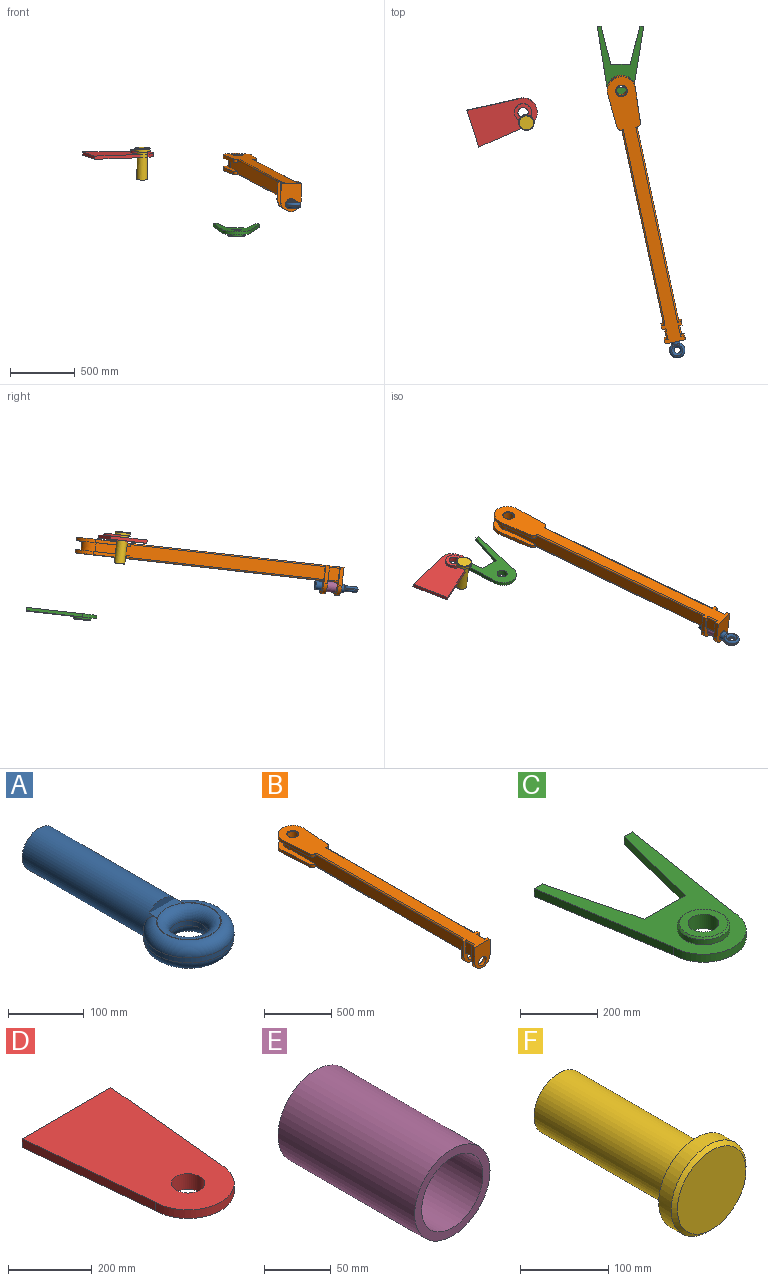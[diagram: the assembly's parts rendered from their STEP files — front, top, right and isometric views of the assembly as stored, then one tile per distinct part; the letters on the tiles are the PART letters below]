
ASSEMBLY  parts=6 mates=6
PART A: 12 faces, bbox 129.9x344.9x64 mm
  f0: cylinder r=32mm len=244.42mm, axis (0,1,0), area 46375.5mm2, adj f1,f2,f3,f4,f5,f6,f9,f11
  f1: plane 48.29x11mm, normal (0,-1,0), area 368.4mm2, adj f0,f5
  f2: plane 48.29x11mm, normal (0,-1,0), area 368.4mm2, adj f0,f6
  f3: plane 64x64mm, normal (0,1,0), area 3217mm2, adj f0
  f4: cylinder r=60mm len=120mm, axis (0,0,1), area 2477.5mm2, adj f0,f9,f11
  f5: plane 93x86mm, normal (0,0,-1), area 720mm2, adj f0,f1,f10,f11
  f6: plane 93x86mm, normal (0,0,1), area 720mm2, adj f0,f2,f8,f9
  f7: cylinder r=25mm len=50mm, axis (0,0,1), area 1256.6mm2, adj f8,f10
  f8: torus R=42mm, axis (0,0,1), area 5231.1mm2, adj f6,f7
  f9: torus R=43mm, axis (0,0,1), area 7473.2mm2, adj f0,f4,f6
  f10: torus R=42mm, axis (0,0,1), area 5231.1mm2, adj f5,f7
  f11: torus R=43mm, axis (0,0,1), area 7473.2mm2, adj f0,f4,f5
PART B: 63 faces, bbox 220x2110x220 mm
  f0: plane 100x85mm, normal (1,0,0), area 8500mm2, adj f23,f26,f36,f37
  f1: plane 100x85mm, normal (-1,0,0), area 8500mm2, adj f23,f26,f35,f38
  f2: plane 100x85mm, normal (0,0,-1), area 8500mm2, adj f23,f26,f35,f36
  f3: plane 1824.08x100mm, normal (1,0,0), area 174335.4mm2, adj f6,f12,f13,f18,f19,f22,f31,f33
  f4: plane 1824.08x100mm, normal (-1,0,0), area 174335.4mm2, adj f6,f12,f14,f18,f20,f22,f32,f34
  f5: plane 1965x220mm, normal (0,0,-1), area 227854.4mm2, adj f15,f16,f17,f19,f20,f22,f32,f33
  f6: cylinder r=67.5mm len=135mm, axis (0,0,1), area 19341.1mm2, adj f3,f4,f12,f18
  f7: plane 2110x220mm, normal (0,0,1), area 245919.5mm2, adj f8,f9,f10,f11,f13,f14,f22,f23
  f8: plane 220x160mm, normal (0,-1,0), area 27426.5mm2, adj f7,f27,f28,f29,f39
  f9: plane 257.39x25mm, normal (1,-0.07,0), area 6449.1mm2, adj f7,f11,f12,f44
  f10: plane 257.39x25mm, normal (-1,-0.07,0), area 6449.1mm2, adj f7,f11,f12,f43
  f11: cylinder r=110mm len=220mm, axis (0,0,1), area 9371.6mm2, adj f7,f9,f10,f12
  f12: plane 410x220mm, normal (0,0,-1), area 35211.4mm2, adj f3,f4,f6,f9,f10,f11,f13,f14
  f13: plane 25x11.93mm, normal (0,-1,0), area 69.8mm2, adj f3,f7,f12,f31,f44
  f14: plane 25x11.93mm, normal (0,-1,0), area 69.8mm2, adj f4,f7,f12,f34,f43
  f15: plane 264.61x25mm, normal (-1,-0.07,0), area 6630.4mm2, adj f5,f17,f18,f42
  f16: plane 257.39x25mm, normal (1,-0.07,0), area 6449.1mm2, adj f5,f17,f18,f41
  f17: cylinder r=110mm len=220mm, axis (0,0,-1), area 9190.9mm2, adj f5,f15,f16,f18
  f18: plane 410x220mm, normal (0,0,1), area 35246.3mm2, adj f3,f4,f6,f15,f16,f17,f19,f20
  f19: plane 25x11.93mm, normal (0,-1,0), area 69.8mm2, adj f3,f5,f18,f33,f41
  f20: plane 25x11.96mm, normal (0,-1,0), area 70.4mm2, adj f4,f5,f18,f32,f42
  f21: cylinder r=40mm len=110mm, axis (0,0,1), area 27646mm2, adj f45,f46
  f22: plane 220x160mm, normal (0,1,0), area 13112.4mm2, adj f3,f4,f5,f7,f24,f25,f30,f31
  f23: plane 220x160mm, normal (0,-1,0), area 13112.4mm2, adj f0,f1,f2,f7,f24,f25,f30,f35
  f24: plane 140x30mm, normal (-1,0,0), area 4200mm2, adj f7,f22,f23,f40
  f25: plane 140x30mm, normal (1,0,0), area 4200mm2, adj f7,f22,f23,f40
  f26: plane 220x160mm, normal (0,1,0), area 13112.4mm2, adj f0,f1,f2,f7,f27,f28,f29,f35
  f27: plane 140x30mm, normal (-1,0,0), area 4200mm2, adj f7,f8,f26,f39
  f28: plane 140x30mm, normal (1,0,0), area 4200mm2, adj f7,f8,f26,f39
  f29: cylinder r=40mm len=80mm, axis (0,-1,0), area 7539.8mm2, adj f8,f26
  f30: cylinder r=40mm len=80mm, axis (0,-1,0), area 7539.8mm2, adj f22,f23
  f31: cylinder r=10mm len=1555mm, axis (0,1,0), area 24425.9mm2, adj f3,f7,f13,f22
  f32: cylinder r=10mm len=1555mm, axis (0,1,0), area 24425.9mm2, adj f4,f5,f20,f22
  f33: cylinder r=10mm len=1555mm, axis (0,-1,0), area 24425.9mm2, adj f3,f5,f19,f22
  f34: cylinder r=10mm len=1555mm, axis (0,-1,0), area 24425.9mm2, adj f4,f7,f14,f22
  f35: cylinder r=10mm len=85mm, axis (0,1,0), area 1335.2mm2, adj f1,f2,f23,f26
  f36: cylinder r=10mm len=85mm, axis (0,-1,0), area 1335.2mm2, adj f0,f2,f23,f26
  f37: cylinder r=10mm len=85mm, axis (0,1,0), area 1335.2mm2, adj f0,f7,f23,f26
  f38: cylinder r=10mm len=85mm, axis (0,-1,0), area 1335.2mm2, adj f1,f7,f23,f26
  f39: cylinder r=80mm len=160mm, axis (0,-1,0), area 7539.8mm2, adj f8,f26,f27,f28
  f40: cylinder r=80mm len=160mm, axis (0,-1,0), area 7539.8mm2, adj f22,f23,f24,f25
  f41: cylinder r=30mm len=29.93mm, axis (0,0,-1), area 1128.2mm2, adj f5,f16,f18,f19
  f42: cylinder r=30mm len=29.93mm, axis (0,0,-1), area 1127.5mm2, adj f5,f15,f18,f20
  f43: cylinder r=30mm len=29.93mm, axis (0,0,1), area 1128.2mm2, adj f7,f10,f12,f14
  f44: cylinder r=30mm len=29.93mm, axis (0,0,1), area 1128.2mm2, adj f7,f9,f12,f13
  f45: cone r=40mm half-angle=45deg, axis (0,0,-1), area 1888.2mm2, adj f5,f21
  f46: cone r=40mm half-angle=45deg, axis (0,0,1), area 1888.2mm2, adj f7,f21
  f47: plane 100x100mm, normal (0,1,0), area 10000mm2, adj f49,f50,f51,f52
  f48: plane 100x100mm, normal (0,-1,0), area 10000mm2, adj f49,f50,f51,f52
  f49: plane 100x85mm, normal (-1,0,0), area 8500mm2, adj f47,f48,f50,f52
  f50: plane 100x85mm, normal (0,0,-1), area 8500mm2, adj f47,f48,f49,f51
  f51: plane 100x85mm, normal (1,0,0), area 8500mm2, adj f47,f48,f50,f52
  f52: plane 100x85mm, normal (0,0,1), area 8500mm2, adj f47,f48,f49,f51
  f53: plane 100x100mm, normal (0,1,0), area 10000mm2, adj f59,f60,f61,f62
  f54: plane 100x15mm, normal (0,-1,0), area 1500mm2, adj f55,f59,f61,f62
  f55: plane 254.65x100mm, normal (0,0,1), area 23932mm2, adj f54,f56,f59,f61
  f56: cylinder r=67.5mm len=100mm, axis (0,0,1), area 7882.9mm2, adj f55,f57,f59,f61
  f57: plane 254.65x100mm, normal (0,0,-1), area 23932mm2, adj f56,f58,f59,f61
  f58: plane 100x15mm, normal (0,-1,0), area 1500mm2, adj f57,f59,f60,f61
  f59: plane 1809.65x100mm, normal (-1,0,0), area 173325.8mm2, adj f53,f54,f55,f56,f57,f58,f60,f62
  f60: plane 1555x100mm, normal (0,0,-1), area 155500mm2, adj f53,f58,f59,f61
  f61: plane 1809.65x100mm, normal (1,0,0), area 173325.8mm2, adj f53,f54,f55,f56,f57,f58,f60,f62
  f62: plane 1555x100mm, normal (0,0,1), area 155500mm2, adj f53,f54,f59,f61
PART C: 14 faces, bbox 360x550x46 mm
  f0: plane 30x25mm, normal (0,1,0), area 750mm2, adj f4,f5,f6,f9
  f1: cylinder r=110mm len=220mm, axis (0,0,-1), area 8639.4mm2, adj f2,f4,f5,f6
  f2: plane 440x70mm, normal (0.99,-0.16,0), area 11138.3mm2, adj f1,f3,f5,f6
  f3: plane 30x25mm, normal (0,1,0), area 750mm2, adj f2,f5,f6,f8
  f4: plane 440x70mm, normal (-0.99,-0.16,0), area 11138.3mm2, adj f0,f1,f5,f6
  f5: plane 550x360mm, normal (0,0,1), area 65296mm2, adj f0,f1,f2,f3,f4,f7,f8,f9
  f6: plane 550x360mm, normal (0,0,-1), area 74583.3mm2, adj f0,f1,f2,f3,f4,f7,f8,f9
  f7: plane 150x25mm, normal (0,1,0), area 3750mm2, adj f5,f6,f8,f9
  f8: plane 297.76x75mm, normal (-0.97,0.24,0), area 7676.6mm2, adj f3,f5,f6,f7
  f9: plane 297.76x75mm, normal (0.97,0.24,0), area 7676.6mm2, adj f0,f5,f6,f7
  f10: cylinder r=67.5mm len=135mm, axis (0,0,-1), area 6785.8mm2, adj f5,f13
  f11: plane 125x125mm, normal (0,0,1), area 7245.3mm2, adj f12,f13
  f12: cylinder r=40mm len=80mm, axis (0,0,1), area 11561.1mm2, adj f6,f11
  f13: cone r=62.5mm half-angle=45deg, axis (0,0,-1), area 2887.9mm2, adj f10,f11
PART D: 9 faces, bbox 300x520x46 mm
  f0: cylinder r=110mm len=220mm, axis (0,0,-1), area 8639.4mm2, adj f1,f2,f4,f5
  f1: plane 520x300mm, normal (0,0,1), area 120580.1mm2, adj f0,f3,f4,f5,f8
  f2: plane 520x300mm, normal (0,0,-1), area 111292.8mm2, adj f0,f3,f4,f5,f6
  f3: plane 300x25mm, normal (0,1,0), area 7500mm2, adj f1,f2,f4,f5
  f4: plane 410x40mm, normal (-1,-0.1,0), area 10298.7mm2, adj f0,f1,f2,f3
  f5: plane 410x40mm, normal (1,-0.1,0), area 10298.7mm2, adj f0,f1,f2,f3
  f6: cylinder r=67.5mm len=135mm, axis (0,0,1), area 8906.4mm2, adj f2,f7
  f7: plane 135x135mm, normal (0,0,-1), area 9287.3mm2, adj f6,f8
  f8: cylinder r=40mm len=80mm, axis (0,0,-1), area 11561.1mm2, adj f1,f7
PART E: 4 faces, bbox 80x145x80 mm
  f0: cylinder r=32.5mm len=145mm, axis (0,1,0), area 29609.5mm2, adj f2,f3
  f1: cylinder r=40mm len=145mm, axis (0,1,0), area 36442.5mm2, adj f2,f3
  f2: plane 80x80mm, normal (0,-1,0), area 1708.2mm2, adj f0,f1
  f3: plane 80x80mm, normal (0,1,0), area 1708.2mm2, adj f0,f1
PART F: 8 faces, bbox 120x245x120 mm
  f0: cylinder r=40mm len=220mm, axis (0,1,0), area 55292mm2, adj f1,f4
  f1: plane 80x80mm, normal (0,1,0), area 4680.2mm2, adj f0,f6
  f2: cylinder r=60mm len=120mm, axis (0,1,0), area 7539.8mm2, adj f4,f5
  f3: plane 110x110mm, normal (0,-1,0), area 9503.3mm2, adj f5
  f4: plane 120x120mm, normal (0,1,0), area 6283.2mm2, adj f0,f2
  f5: cone r=55mm half-angle=45deg, axis (0,1,0), area 2554.7mm2, adj f2,f3
  f6: cylinder r=10.5mm len=70mm, axis (0,1,0), area 4618.1mm2, adj f1,f7
  f7: plane 21x21mm, normal (0,1,0), area 346.4mm2, adj f6
PLACE A rot(axis=(0.47,-0.05,0.88),13.6deg) t=(923.22,669.84,-423.47)mm
PLACE B rot(axis=(0.47,0.01,0.89),13.6deg) t=(733,1552.62,-223.21)mm
PLACE C rot(axis=(0,-1,-0.05),179.3deg) t=(517.72,2583.19,-646.71)mm
PLACE D rot(axis=(-0.81,0.59,0.04),175.3deg) t=(-237.24,2353.98,-49.34)mm
PLACE E rot(axis=(0.47,0.01,0.89),13.6deg) t=(924.88,662.12,-424.35)mm
PLACE F rot(axis=(-0.99,-0.11,0.11),84.4deg) t=(-212.55,2285.01,-134.22)mm
MATE pin_slot D.f0 <-> B.f6  axis (-0.01,0.11,-0.99) through (-237.4,2355.35,-61.76)mm
MATE revolute A.f0 <-> E.f0  axis (-0.21,0.97,0.11) through (924.88,662.12,-424.35)mm
MATE cylindrical A.f0 <-> E.f0  axis (-0.21,0.97,0.11) through (924.88,662.12,-424.35)mm
MATE fastened E.f0 <-> B.f29  axis (-0.21,0.97,0.11) through (909.78,732.58,-416.39)mm
MATE cylindrical C.f1 <-> B.f6  axis (0.01,-0.11,0.99) through (517.88,2581.82,-634.28)mm
MATE pin_slot F.f0 <-> D.f0  axis (-0.01,0.11,-0.99) through (-211.11,2272.98,-24.89)mm
